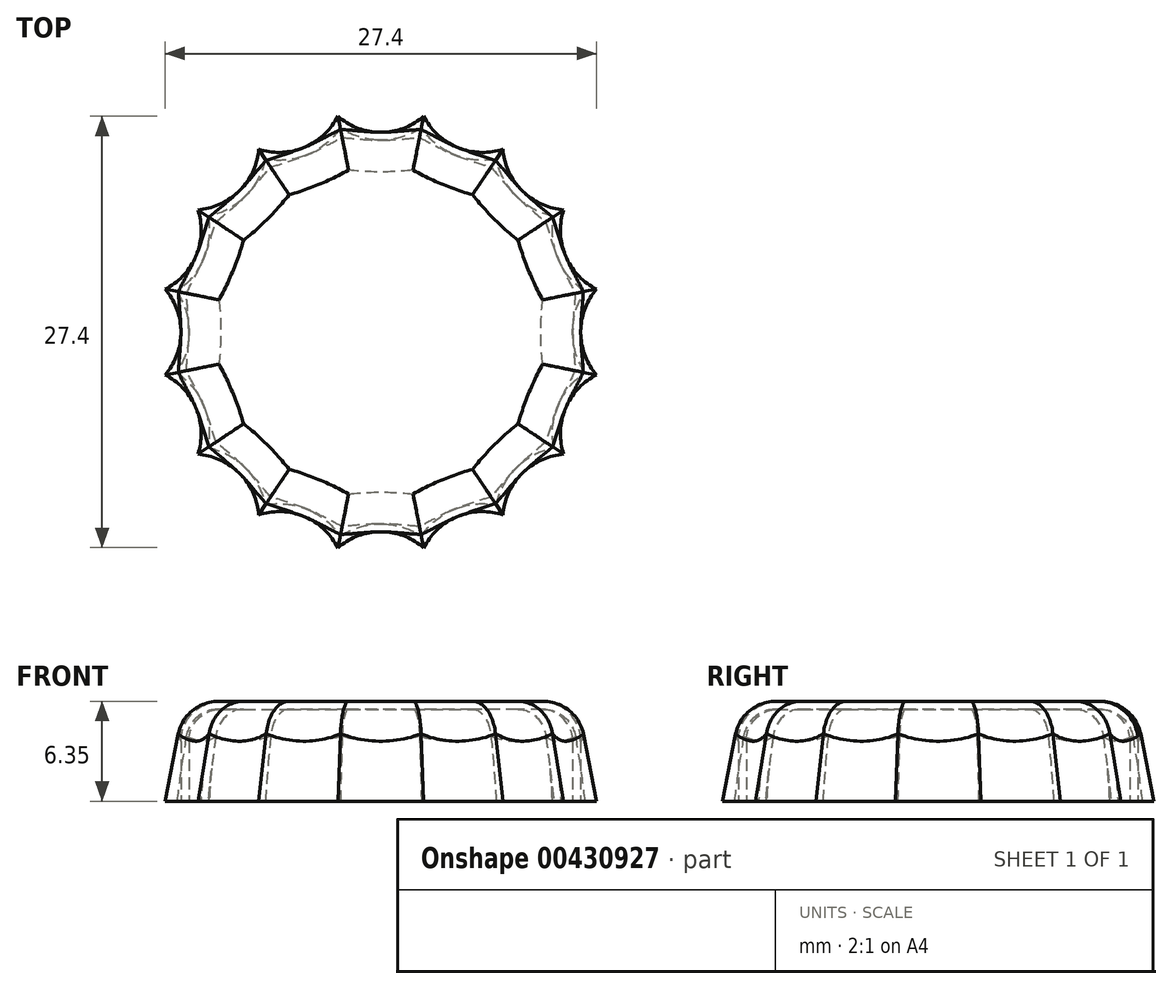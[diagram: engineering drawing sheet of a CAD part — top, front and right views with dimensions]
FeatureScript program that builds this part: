
annotation { "Feature Type Name" : "Feature", "Feature Type Description" : "" }
export const myFeature = defineFeature(function(context is Context, id is Id, definition is map)
    precondition{}
    {
        {
            var Q0;
            Q0=qCreatedBy(makeId("Top.planeOp"),FACE);
            var sketch = newSketch(context, id + "F0", { "sketchPlane" : qUnion([Q0])});
            skCircle(sketch, "E0", {"center": v(0, 0) * mm, "radius": 12.7 * mm, "construction": true});
            skCircle(sketch, "E1.0", {"center": v(0, 0) * mm, "radius": 13.97 * mm});
            skArc(sketch, "E2", {"start": v(-2.73, 13.7) * mm, "mid": v(0, 12.7) * mm, "end": v(2.73, 13.7) * mm});
            skArc(sketch, "E3.1.0", {"start": v(-7.76, 11.62) * mm, "mid": v(-4.86, 11.73) * mm, "end": v(-2.73, 13.7) * mm});
            skArc(sketch, "E3.2.0", {"start": v(-11.62, 7.76) * mm, "mid": v(-8.98, 8.98) * mm, "end": v(-7.76, 11.62) * mm});
            skArc(sketch, "E3.3.0", {"start": v(-13.7, 2.73) * mm, "mid": v(-11.73, 4.86) * mm, "end": v(-11.62, 7.76) * mm});
            skArc(sketch, "E3.4.0", {"start": v(-13.7, -2.73) * mm, "mid": v(-12.7, 0) * mm, "end": v(-13.7, 2.73) * mm});
            skArc(sketch, "E3.5.0", {"start": v(-11.62, -7.76) * mm, "mid": v(-11.73, -4.86) * mm, "end": v(-13.7, -2.73) * mm});
            skArc(sketch, "E3.6.0", {"start": v(-7.76, -11.62) * mm, "mid": v(-8.98, -8.98) * mm, "end": v(-11.62, -7.76) * mm});
            skArc(sketch, "E3.7.0", {"start": v(-2.73, -13.7) * mm, "mid": v(-4.86, -11.73) * mm, "end": v(-7.76, -11.62) * mm});
            skArc(sketch, "E3.8.0", {"start": v(2.73, -13.7) * mm, "mid": v(0, -12.7) * mm, "end": v(-2.73, -13.7) * mm});
            skArc(sketch, "E3.9.0", {"start": v(7.76, -11.62) * mm, "mid": v(4.86, -11.73) * mm, "end": v(2.73, -13.7) * mm});
            skArc(sketch, "E3.10.0", {"start": v(11.62, -7.76) * mm, "mid": v(8.98, -8.98) * mm, "end": v(7.76, -11.62) * mm});
            skArc(sketch, "E3.11.0", {"start": v(13.7, -2.73) * mm, "mid": v(11.73, -4.86) * mm, "end": v(11.62, -7.76) * mm});
            skArc(sketch, "E3.12.0", {"start": v(13.7, 2.73) * mm, "mid": v(12.7, 0) * mm, "end": v(13.7, -2.73) * mm});
            skArc(sketch, "E3.13.0", {"start": v(11.62, 7.76) * mm, "mid": v(11.73, 4.86) * mm, "end": v(13.7, 2.73) * mm});
            skArc(sketch, "E3.14.0", {"start": v(7.76, 11.62) * mm, "mid": v(8.98, 8.98) * mm, "end": v(11.62, 7.76) * mm});
            skArc(sketch, "E3.15.0", {"start": v(2.73, 13.7) * mm, "mid": v(4.86, 11.73) * mm, "end": v(7.76, 11.62) * mm});
            skSolve(sketch);
        }
        {
            var Q0;
            Q0=makeQuery(id+"F0.imprint","IMPRINT",FACE,{"disambiguationData":[TD([[makeQuery(id+"F0.imprint","IMPRINT",EDGE,{"derivedFrom":sQuery(id+"F0.wireOp",EDGE,"E2")}),-1.0]])]});
            cPlane(context, id + "F1", {"entities" : qUnion([Q0]), "cplaneType" : CPlaneType.OFFSET, "offset" : 6.35 * mm, "width" : 152.4 * mm, "height" : 152.4 * mm});
        }
        {
            var Q0;
            Q0=qCreatedBy(id+"F1.planeOp",FACE);
            var sketch = newSketch(context, id + "F2", { "sketchPlane" : qUnion([Q0])});
            skCircle(sketch, "E4.0", {"center": v(0, 0) * mm, "radius": 12.7 * mm});
            skSolve(sketch);
        }
        {
            var Q0;
            Q0=makeQuery(id+"F0.imprint","IMPRINT",FACE,{"disambiguationData":[TD([[makeQuery(id+"F0.imprint","IMPRINT",EDGE,{"derivedFrom":sQuery(id+"F0.wireOp",EDGE,"E2")}),-1.0]])]});
            var Q1;
            Q1=makeQuery(id+"F2.imprint","IMPRINT",FACE,{"disambiguationData":[TD([[makeQuery(id+"F2.imprint","IMPRINT",EDGE,{"derivedFrom":sQuery(id+"F2.wireOp",EDGE,"E4.0")}),1.0]])]});
            loft(context, id + "F3", {"sheetProfilesArray" : [{ "sheetProfileEntities" : qUnion([Q0]) }, { "sheetProfileEntities" : qUnion([Q1]) }]});
        }
        {
            var Q0;
            Q0=makeQuery(id+"F3.opLoft","CAP_FACE",FACE,{"disambiguationData":[OSD([makeQuery(id+"F2.imprint","IMPRINT",FACE,{"disambiguationData":[TD([[makeQuery(id+"F2.imprint","IMPRINT",EDGE,{"derivedFrom":sQuery(id+"F2.wireOp",EDGE,"E4.0")}),1.0]])]})])],"isStart":true});
            fillet(context, id + "F4", {"entities" : qUnion([Q0]), "radius" : 2.54 * mm, "tangentPropagation" : true, "allowEdgeOverflow" : false});
        }
        {
            var Q0;
            Q0=makeQuery(id+"F3.opLoft","CAP_FACE",FACE,{"disambiguationData":[OSD([makeQuery(id+"F0.imprint","IMPRINT",FACE,{"disambiguationData":[TD([[makeQuery(id+"F0.imprint","IMPRINT",EDGE,{"derivedFrom":sQuery(id+"F0.wireOp",EDGE,"E2")}),-1.0]])]})])],"isStart":true});
            shell(context, id + "F5", {"entities" : qUnion([Q0]), "thickness" : 0.5 * mm});
        }
    });
